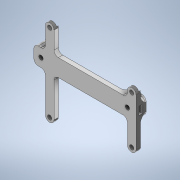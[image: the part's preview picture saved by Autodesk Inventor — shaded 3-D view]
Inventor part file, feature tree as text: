
AUTODESK INVENTOR PART (.ipt)
format: ipt  version: 2020 (Build 240168000, 168)  size: 658,432 bytes
history: native  units: mm
features: projected_geometry x19, extrude x11, sketch x10, fillet x3
ambient origin geometry x8: Origin, YZ Plane, XZ Plane, XY Plane, X Axis, Y Axis, Z Axis, Center Point
bodies: Solid1 (feature_tree)
feature tree (43):
  extrude  "Extrusion1"  Depth=3.0mm
  extrude  "Extrusion2"  TaperAngle=0.0deg  [1 undecoded]
  fillet  "Fillet1"  Radius=60.0mm
  extrude  "Extrusion3"  Depth=3.0mm
  extrude  "Extrusion4"  Depth=3.0mm
  extrude  "Extrusion5"  Depth=10.5mm
  extrude  "Extrusion6"  Depth=21.0mm
  extrude  "Extrusion9"  Depth=35.0mm
  extrude  "Extrusion10"  Depth=57.0mm
  extrude  "Extrusion11"  Depth=60.0mm
  extrude  "Extrusion12"  Depth=2.0mm
  fillet  "Fillet5"  Radius=6.0mm
  extrude  "Extrusion13"  Depth=2.0mm
  fillet  "Fillet6"  Radius=6.0mm
  sketch  "Sketch1"  dims[d0=3.0mm d1=3.0mm]
  sketch  "Sketch2"  dims[d2=0.0mm d3=0.0mm d4=60.0mm]
  sketch  "Sketch4"  dims[d6=3.0mm d7=3.0mm]
  projected_geometry  "Projected Loop1"
  sketch  "Sketch5"  dims[d8=3.0mm d9=3.0mm]
  sketch  "Sketch6"  dims[d10=33.0mm d11=10.5mm]
  projected_geometry  "Projected Loop4"
  projected_geometry  "Projected Loop5"
  projected_geometry  "Projected Loop6"
  projected_geometry  "Projected Loop7"
  projected_geometry  "Projected Loop8"
  sketch  "Sketch9"  dims[d12=54.0mm d13=21.0mm]
  projected_geometry  "Projected Loop9"
  projected_geometry  "Projected Loop10"
  projected_geometry  "Projected Loop11"
  sketch  "Sketch10"  dims[d14=35.0mm d15=35.0mm]
  projected_geometry  "Projected Loop12"
  sketch  "Sketch11"  dims[d16=57.0mm d17=57.0mm]
  projected_geometry  "Projected Loop13"
  projected_geometry  "Projected Loop14"
  sketch  "Sketch12"  dims[d18=63.0mm d19=60.0mm]
  projected_geometry  "Projected Loop15"
  projected_geometry  "Projected Loop16"
  projected_geometry  "Projected Loop17"
  sketch  "Sketch13"  dims[d20=36.0mm d22=3.0mm d23=6.0mm d24=8.0mm d25=6.0mm d26=39.0mm d27=25.5mm d28=4.0mm d29=4.0mm d30=0.0mm d31=5.5mm d32=5.5mm d33=2.0mm d34=0.0mm d35=3.0mm d36=5.5mm d37=5.5mm d38=5.5mm d39=5.5mm d40=2.0mm d41=0.0mm d42=32.0mm d43=1.0mm d44=0.0mm d45=5.6mm d46=5.6mm d48=5.6mm d49=5.6mm d50=2.0mm d51=0.0mm d52=66.0mm d53=12.0mm d54=4.0mm d55=4.0mm d56=4.0mm d57=0.0mm d72=5.6mm d73=3.0mm d74=5.6mm d75=3.0mm d76=3.0mm d77=5.6mm d78=3.0mm d79=2.4mm d80=5.65mm d81=1.5mm d83=2.0mm d84=6.7mm d85=0.0mm d86=7.7mm d87=0.0mm d88=120.0deg d89=120.0deg d90=60.0deg d91=60.0deg d92=7.7mm d93=0.0mm d95=2.5mm d96=2.5mm d97=7.7mm d98=0.0mm d99=3.0mm d100=150.0deg d101=2.0mm d102=60.0deg d103=90.0deg d104=7.7mm d105=0.0mm d106=2.0mm]
  projected_geometry  "Projected Loop18"
  projected_geometry  "Projected Loop19"
  projected_geometry  "Projected Loop20"
  projected_geometry  "Projected Loop21"
note: 1 required parameter value undecoded (feature->parameter linkage not recoverable at this tier; creation-order binding heuristic only, values carry confidence <= 0.55)
